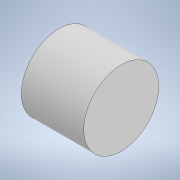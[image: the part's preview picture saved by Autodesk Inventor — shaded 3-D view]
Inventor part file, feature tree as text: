
AUTODESK INVENTOR PART (.ipt)
format: ipt  version: 2022 (Build 260153000, 153)  size: 89,600 bytes
history: native  units: in
note: dims shown in document units (in); Inventor stores cm internally (conversion verified against a paired STEP export)
features: extrude x1, sketch x1
ambient origin geometry x8: Origin, YZ Plane, XZ Plane, XY Plane, X Axis, Y Axis, Z Axis, Center Point
bodies: Solid1 (feature_tree)
feature tree (2):
  extrude  "Extrusion1"  Depth=0.25in TaperAngle=0.0deg
  sketch  "Sketch1"  dims[d0=0.3in d1=0.25in d2=0.0in]
